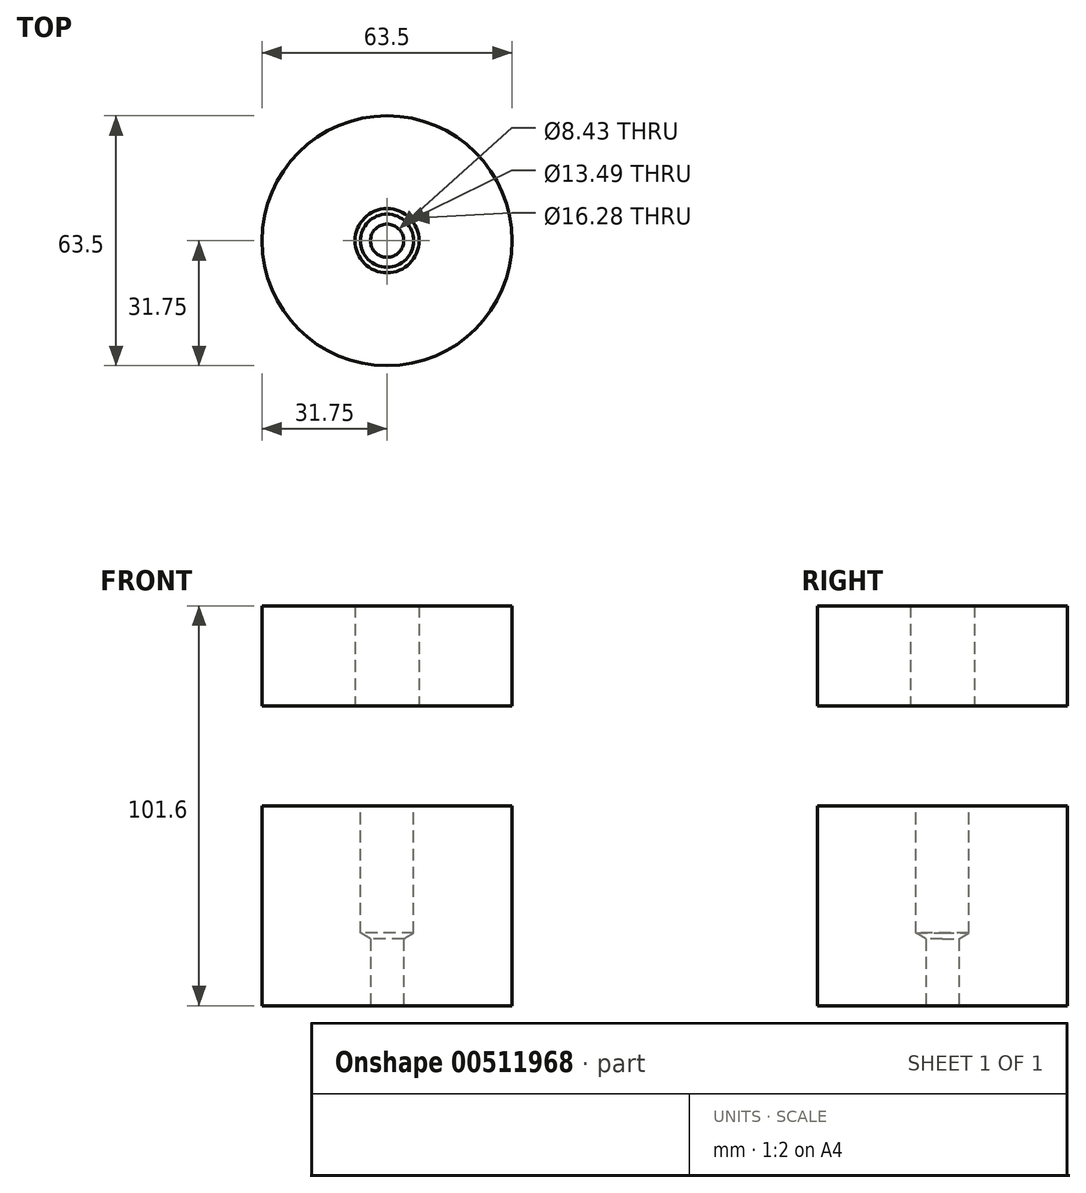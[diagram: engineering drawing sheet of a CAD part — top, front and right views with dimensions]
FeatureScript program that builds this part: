
annotation { "Feature Type Name" : "Feature", "Feature Type Description" : "" }
export const myFeature = defineFeature(function(context is Context, id is Id, definition is map)
    precondition{}
    {
        {
            var Q0;
            Q0=qCreatedBy(makeId("Top.planeOp"),FACE);
            var sketch = newSketch(context, id + "F0", { "sketchPlane" : qUnion([Q0])});
            skCircle(sketch, "E0", {"center": v(0, 0) * mm, "radius": 31.75 * mm});
            skSolve(sketch);
        }
        {
            var Q0;
            Q0 = qSketchRegion(id + "F0", true);
            extrude(context, id + "F1", {"entities" : qUnion([Q0]), "depth" : 50.8 * mm});
        }
        {
            var Q0;
            Q0=sQuery(id+"F0.wireOp",VERTEX,"E0.center");
            var Q1;
            Q1=makeQuery(id+"F1.opExtrude","SWEPT_BODY",BODY,{"disambiguationData":[OSD([sQuery(id+"F0.wireOp",EDGE,"E0")])]});
            hole(context, id + "F2", {"style" : HoleStyle.SIMPLE, "endStyle" : HoleEndStyle.THROUGH, "oppositeDirection" : true, "standardTappedOrClearance" : lookupTablePath({ "standard" : "ANSI", "fit" : "Normal (ASME)", "size" : "5/16", "type" : "Clearance" }), "standardBlindInLast" : lookupTablePath({ "fit" : "Free", "standard" : "ANSI", "size" : "5/16", "type" : "Clearance" }), "holeDiameter" : 8.43 * mm, "isTappedThrough" : true, "tappedDepth" : 12.7 * mm, "tapClearance" : 3, "locations" : qUnion([Q0]), "scope" : qUnion([Q1])});
        }
        {
            var Q0;
            Q0=makeQuery(id+"F1.opExtrude","CAP_FACE",FACE,{"disambiguationData":[OSD([sQuery(id+"F0.wireOp",EDGE,"E0")])],"isStart":false});
            var sketch = newSketch(context, id + "F3", { "sketchPlane" : qUnion([Q0])});
            skPoint(sketch, "E1", {"position": v(0, 0) * mm});
            skSolve(sketch);
        }
        {
            var Q0;
            Q0=sQuery(id+"F3.wireOp",VERTEX,"E1");
            var Q1;
            Q1=makeQuery(id+"F1.opExtrude","SWEPT_BODY",BODY,{"disambiguationData":[OSD([sQuery(id+"F0.wireOp",EDGE,"E0")])]});
            hole(context, id + "F4", {"style" : HoleStyle.SIMPLE, "endStyle" : HoleEndStyle.BLIND, "standardTappedOrClearance" : lookupTablePath({ "standard" : "ANSI", "engagement" : "75%", "pitch" : "11 tpi", "size" : "5/8", "type" : "Tapped" }), "standardBlindInLast" : lookupTablePath({ "standard" : "ANSI", "engagement" : "75%", "pitch" : "11 tpi", "size" : "5/8", "type" : "Tapped" }), "holeDiameter" : 13.5 * mm, "showTappedDepth" : true, "holeDepth" : 32.33 * mm, "isTappedThrough" : true, "tappedDepth" : 25.4 * mm, "tapClearance" : 3, "locations" : qUnion([Q0]), "scope" : qUnion([Q1]), "majorDiameter" : 15.88 * mm});
        }
        {
            var Q0;
            Q0=makeQuery(id+"F1.opExtrude","CAP_FACE",FACE,{"disambiguationData":[OSD([sQuery(id+"F0.wireOp",EDGE,"E0")])],"isStart":false});
            cPlane(context, id + "F5", {"entities" : qUnion([Q0]), "cplaneType" : CPlaneType.OFFSET, "offset" : 25.4 * mm, "width" : 152.4 * mm, "height" : 152.4 * mm});
        }
        {
            var Q0;
            Q0=qCreatedBy(id+"F5.planeOp",FACE);
            var sketch = newSketch(context, id + "F6", { "sketchPlane" : qUnion([Q0])});
            skCircle(sketch, "E2", {"center": v(0, 0) * mm, "radius": 31.75 * mm});
            skSolve(sketch);
        }
        {
            var Q0;
            Q0=makeQuery(id+"F6.imprint","IMPRINT",FACE,{"disambiguationData":[TD([[makeQuery(id+"F6.imprint","IMPRINT",EDGE,{"derivedFrom":sQuery(id+"F6.wireOp",EDGE,"E2")}),1.0]])]});
            extrude(context, id + "F7", {"entities" : qUnion([Q0]), "depth" : 25.4 * mm});
        }
        {
            var Q0;
            Q0=sQuery(id+"F6.wireOp",VERTEX,"E2.center");
            var Q1;
            Q1=makeQuery(id+"F7.opExtrude","SWEPT_BODY",BODY,{"disambiguationData":[OSD([sQuery(id+"F6.wireOp",EDGE,"E2")])]});
            hole(context, id + "F8", {"style" : HoleStyle.SIMPLE, "endStyle" : HoleEndStyle.THROUGH, "oppositeDirection" : true, "standardTappedOrClearance" : lookupTablePath({ "standard" : "ANSI", "fit" : "Close", "size" : "5/8", "type" : "Clearance" }), "standardBlindInLast" : lookupTablePath({ "fit" : "Close", "standard" : "ANSI", "size" : "5/8", "type" : "Clearance" }), "holeDiameter" : 16.28 * mm, "isTappedThrough" : true, "tappedDepth" : 12.7 * mm, "tapClearance" : 3, "locations" : qUnion([Q0]), "scope" : qUnion([Q1])});
        }
    });
